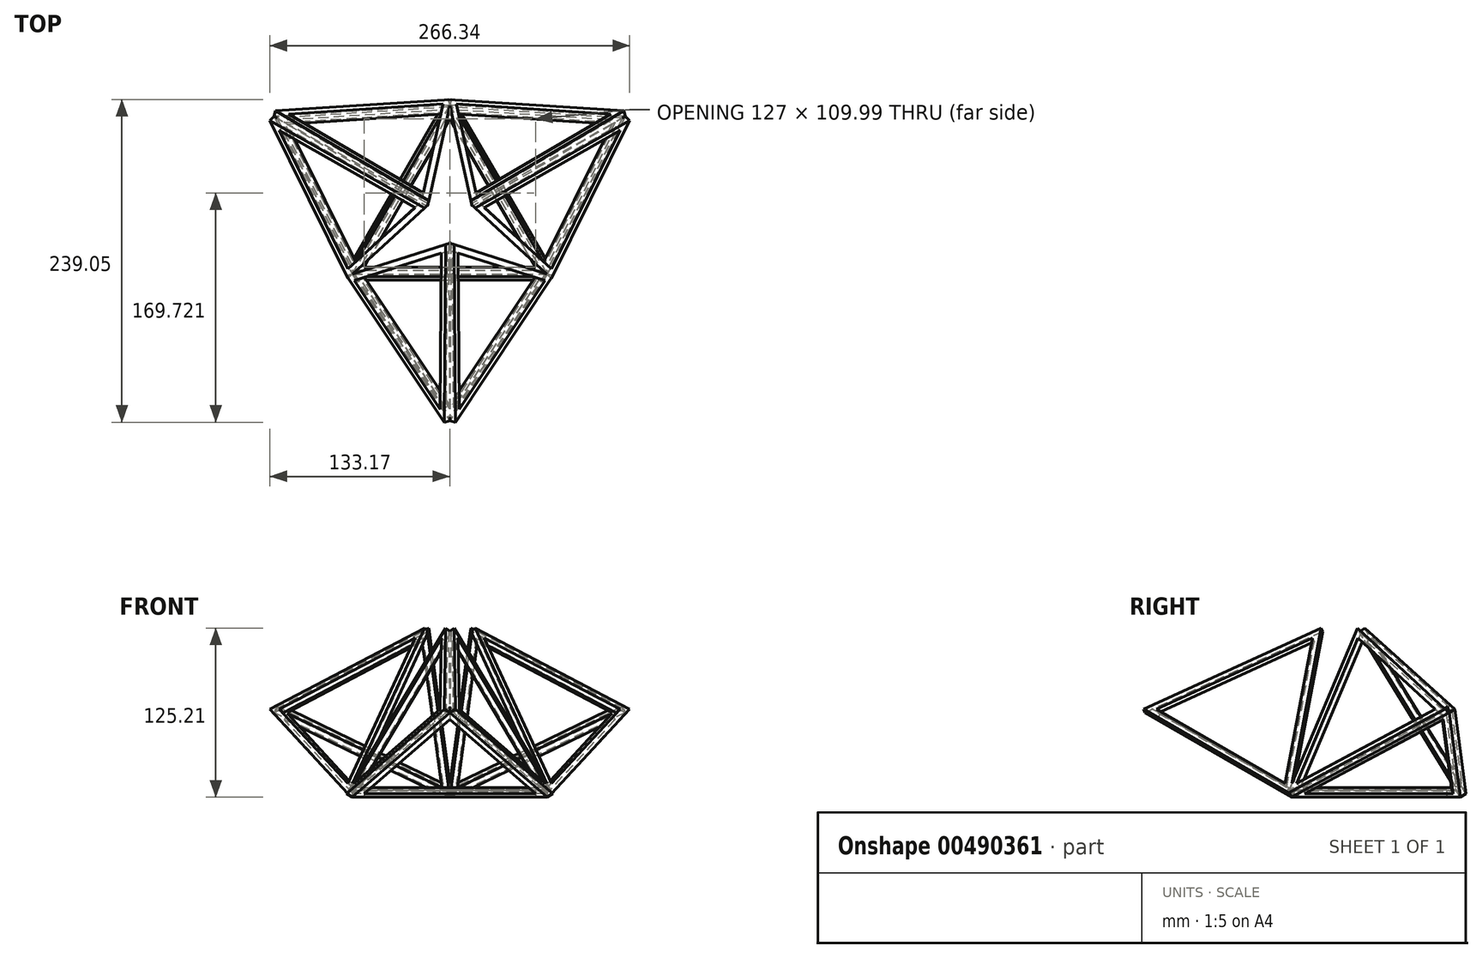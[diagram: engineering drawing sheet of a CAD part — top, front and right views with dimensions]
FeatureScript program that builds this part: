
annotation { "Feature Type Name" : "Feature", "Feature Type Description" : "" }
export const myFeature = defineFeature(function(context is Context, id is Id, definition is map)
    precondition{}
    {
        {
            var Q0;
            Q0=qCreatedBy(makeId("Top.planeOp"),FACE);
            var sketch = newSketch(context, id + "F0", { "sketchPlane" : qUnion([Q0])});
            skLineSegment(sketch, "E0", {"start": v(0, 73.32) * mm, "end": v(-63.5, -36.66) * mm});
            skLineSegment(sketch, "E1", {"start": v(-63.5, -36.66) * mm, "end": v(63.5, -36.66) * mm});
            skLineSegment(sketch, "E2", {"start": v(63.5, -36.66) * mm, "end": v(0, 73.32) * mm});
            skLineSegment(sketch, "E3", {"start": v(0, 83.48) * mm, "end": v(-72.3, -41.74) * mm});
            skLineSegment(sketch, "E4", {"start": v(-72.3, -41.74) * mm, "end": v(72.3, -41.74) * mm});
            skLineSegment(sketch, "E5", {"start": v(72.3, -41.74) * mm, "end": v(0, 83.48) * mm});
            skLineSegment(sketch, "E6", {"start": v(-31.75, 18.33) * mm, "end": v(63.5, -36.66) * mm, "construction": true});
            skLineSegment(sketch, "E7", {"start": v(31.75, 18.33) * mm, "end": v(-63.5, -36.66) * mm, "construction": true});
            skPoint(sketch, "E8", {"position": v(0, 0) * mm});
            skSolve(sketch);
        }
        {
            var Q0;
            Q0 = qSketchRegion(id + "F0", true);
            extrude(context, id + "F1", {"entities" : qUnion([Q0]), "depth" : 5.08 * mm});
        }
        {
            var Q0;
            Q0=makeQuery(id+"F1.opExtrude","CAP_EDGE",EDGE,{"disambiguationData":[OSD([sQuery(id+"F0.wireOp",EDGE,"E3")])],"isStart":true});
            var Q1;
            Q1=qCreatedBy(makeId("Top.planeOp"),FACE);
            cPlane(context, id + "F2", {"entities" : qUnion([Q0, Q1]), "cplaneType" : CPlaneType.LINE_ANGLE, "offset" : 25.4 * mm, "angle" : 30 * degree, "oppositeDirection" : true, "width" : 152.4 * mm, "height" : 152.4 * mm});
        }
        {
            var Q0;
            Q0=qCreatedBy(id+"F2.planeOp",FACE);
            var sketch = newSketch(context, id + "F3", { "sketchPlane" : qUnion([Q0])});
            skLineSegment(sketch, "E9.0", {"start": v(10.03, -80.2) * mm, "end": v(-70.18, 40.1) * mm});
            skLineSegment(sketch, "E10", {"start": v(-30.08, -20.05) * mm, "end": v(-171.97, -114.65) * mm, "construction": true});
            skLineSegment(sketch, "E11", {"start": v(10.03, -80.2) * mm, "end": v(-134.27, -89.51) * mm});
            skLineSegment(sketch, "E12", {"start": v(-134.27, -89.51) * mm, "end": v(-70.18, 40.1) * mm});
            skLineSegment(sketch, "E13", {"start": v(-125.82, -83.88) * mm, "end": v(0.92, -75.7) * mm});
            skLineSegment(sketch, "E14", {"start": v(0.92, -75.7) * mm, "end": v(-69.53, 29.97) * mm});
            skLineSegment(sketch, "E15", {"start": v(-69.53, 29.97) * mm, "end": v(-125.82, -83.88) * mm});
            skSolve(sketch);
        }
        {
            var Q0;
            Q0 = qSketchRegion(id + "F3", true);
            extrude(context, id + "F4", {"entities" : qUnion([Q0]), "oppositeDirection" : true, "depth" : 5.08 * mm});
        }
        {
            var Q0;
            Q0=makeQuery(id+"F1.opExtrude","CAP_EDGE",EDGE,{"disambiguationData":[OSD([sQuery(id+"F0.wireOp",EDGE,"E4")])],"isStart":true});
            var Q1;
            Q1=qCreatedBy(makeId("Top.planeOp"),FACE);
            cPlane(context, id + "F5", {"entities" : qUnion([Q0, Q1]), "cplaneType" : CPlaneType.LINE_ANGLE, "offset" : 25.4 * mm, "angle" : 30 * degree, "oppositeDirection" : true, "width" : 152.4 * mm, "height" : 152.4 * mm});
        }
        {
            var Q0;
            Q0=qCreatedBy(id+"F5.planeOp",FACE);
            var sketch = newSketch(context, id + "F6", { "sketchPlane" : qUnion([Q0])});
            skLineSegment(sketch, "E16.0", {"start": v(72.3, 36.15) * mm, "end": v(0, 161.37) * mm});
            skLineSegment(sketch, "E17", {"start": v(36.15, 98.76) * mm, "end": v(-111.54, 13.5) * mm, "construction": true});
            skLineSegment(sketch, "E18", {"start": v(72.3, 36.15) * mm, "end": v(-72.3, 36.15) * mm});
            skLineSegment(sketch, "E19", {"start": v(-72.3, 36.15) * mm, "end": v(0, 161.37) * mm});
            skLineSegment(sketch, "E20", {"start": v(-63.5, 41.23) * mm, "end": v(63.5, 41.23) * mm});
            skLineSegment(sketch, "E21", {"start": v(63.5, 41.23) * mm, "end": v(0, 151.21) * mm});
            skLineSegment(sketch, "E22", {"start": v(0, 151.21) * mm, "end": v(-63.5, 41.23) * mm});
            skSolve(sketch);
        }
        {
            var Q0;
            Q0 = qSketchRegion(id + "F6", true);
            extrude(context, id + "F7", {"entities" : qUnion([Q0]), "oppositeDirection" : true, "depth" : 5.08 * mm});
        }
        {
            var Q0;
            Q0=makeQuery(id+"F1.opExtrude","CAP_EDGE",EDGE,{"disambiguationData":[OSD([sQuery(id+"F0.wireOp",EDGE,"E5")])],"isStart":true});
            var Q1;
            Q1=qCreatedBy(makeId("Top.planeOp"),FACE);
            cPlane(context, id + "F8", {"entities" : qUnion([Q0, Q1]), "cplaneType" : CPlaneType.LINE_ANGLE, "offset" : 25.4 * mm, "angle" : 30 * degree, "oppositeDirection" : true, "width" : 152.4 * mm, "height" : 152.4 * mm});
        }
        {
            var Q0;
            Q0=qCreatedBy(id+"F8.planeOp",FACE);
            var sketch = newSketch(context, id + "F9", { "sketchPlane" : qUnion([Q0])});
            skLineSegment(sketch, "E23.0", {"start": v(134.27, -89.51) * mm, "end": v(70.18, 40.1) * mm});
            skLineSegment(sketch, "E24", {"start": v(102.23, -24.7) * mm, "end": v(-50.34, -100.14) * mm, "construction": true});
            skLineSegment(sketch, "E25", {"start": v(134.27, -89.51) * mm, "end": v(-10.03, -80.2) * mm});
            skLineSegment(sketch, "E26", {"start": v(-10.03, -80.2) * mm, "end": v(70.18, 40.1) * mm});
            skLineSegment(sketch, "E27", {"start": v(-0.92, -75.7) * mm, "end": v(125.82, -83.88) * mm});
            skLineSegment(sketch, "E28", {"start": v(125.82, -83.88) * mm, "end": v(69.53, 29.97) * mm});
            skLineSegment(sketch, "E29", {"start": v(69.53, 29.97) * mm, "end": v(-0.92, -75.7) * mm});
            skSolve(sketch);
        }
        {
            var Q0;
            Q0 = qSketchRegion(id + "F9", true);
            extrude(context, id + "F10", {"entities" : qUnion([Q0]), "oppositeDirection" : true, "depth" : 5.08 * mm});
        }
        {
            var Q0;
            Q0=makeQuery(id+"F10.opExtrude","SWEPT_BODY",BODY,{"disambiguationData":[OSD([sQuery(id+"F9.wireOp",EDGE,"E23.0"),sQuery(id+"F9.wireOp",EDGE,"E25"),sQuery(id+"F9.wireOp",EDGE,"E26"),sQuery(id+"F9.wireOp",EDGE,"E27"),sQuery(id+"F9.wireOp",EDGE,"E28"),sQuery(id+"F9.wireOp",EDGE,"E29")])]});
            var Q1;
            Q1=makeQuery(id+"F10.opExtrude","CAP_EDGE",EDGE,{"disambiguationData":[OSD([sQuery(id+"F9.wireOp",EDGE,"E23.0")])],"isStart":true});
            transform(context, id + "F11", {"entities" : qUnion([Q0]), "transformType" : TransformType.ROTATION, "transformAxis" : qUnion([Q1]), "angle" : 70 * degree, "oppositeDirection" : true, "makeCopy" : true});
        }
        {
            var Q0;
            Q0=makeQuery(id+"F10.opExtrude","SWEPT_BODY",BODY,{"disambiguationData":[OSD([sQuery(id+"F9.wireOp",EDGE,"E23.0"),sQuery(id+"F9.wireOp",EDGE,"E25"),sQuery(id+"F9.wireOp",EDGE,"E26"),sQuery(id+"F9.wireOp",EDGE,"E27"),sQuery(id+"F9.wireOp",EDGE,"E28"),sQuery(id+"F9.wireOp",EDGE,"E29")])]});
            var Q1;
            Q1=makeQuery(id+"F10.opExtrude","CAP_EDGE",EDGE,{"disambiguationData":[OSD([sQuery(id+"F9.wireOp",EDGE,"E25")])],"isStart":true});
            transform(context, id + "F12", {"entities" : qUnion([Q0]), "transformType" : TransformType.ROTATION, "transformAxis" : qUnion([Q1]), "angle" : 70 * degree, "makeCopy" : true});
        }
        {
            var Q0;
            Q0=makeQuery(id+"F7.opExtrude","SWEPT_BODY",BODY,{"disambiguationData":[OSD([sQuery(id+"F6.wireOp",EDGE,"E16.0"),sQuery(id+"F6.wireOp",EDGE,"E18"),sQuery(id+"F6.wireOp",EDGE,"E19"),sQuery(id+"F6.wireOp",EDGE,"E20"),sQuery(id+"F6.wireOp",EDGE,"E21"),sQuery(id+"F6.wireOp",EDGE,"E22")])]});
            var Q1;
            Q1=makeQuery(id+"F7.opExtrude","CAP_EDGE",EDGE,{"disambiguationData":[OSD([sQuery(id+"F6.wireOp",EDGE,"E19")])],"isStart":true});
            transform(context, id + "F13", {"entities" : qUnion([Q0]), "transformType" : TransformType.ROTATION, "transformAxis" : qUnion([Q1]), "angle" : 70 * degree, "makeCopy" : true});
        }
        {
            var Q0;
            Q0=makeQuery(id+"F7.opExtrude","SWEPT_BODY",BODY,{"disambiguationData":[OSD([sQuery(id+"F6.wireOp",EDGE,"E16.0"),sQuery(id+"F6.wireOp",EDGE,"E18"),sQuery(id+"F6.wireOp",EDGE,"E19"),sQuery(id+"F6.wireOp",EDGE,"E20"),sQuery(id+"F6.wireOp",EDGE,"E21"),sQuery(id+"F6.wireOp",EDGE,"E22")])]});
            var Q1;
            Q1=makeQuery(id+"F7.opExtrude","CAP_EDGE",EDGE,{"disambiguationData":[OSD([sQuery(id+"F6.wireOp",EDGE,"E16.0")])],"isStart":true});
            transform(context, id + "F14", {"entities" : qUnion([Q0]), "transformType" : TransformType.ROTATION, "transformAxis" : qUnion([Q1]), "angle" : 70 * degree, "oppositeDirection" : true, "makeCopy" : true});
        }
        {
            var Q0;
            Q0=makeQuery(id+"F4.opExtrude","SWEPT_BODY",BODY,{"disambiguationData":[OSD([sQuery(id+"F3.wireOp",EDGE,"E9.0"),sQuery(id+"F3.wireOp",EDGE,"E11"),sQuery(id+"F3.wireOp",EDGE,"E12"),sQuery(id+"F3.wireOp",EDGE,"E13"),sQuery(id+"F3.wireOp",EDGE,"E14"),sQuery(id+"F3.wireOp",EDGE,"E15")])]});
            var Q1;
            Q1=makeQuery(id+"F4.opExtrude","CAP_EDGE",EDGE,{"disambiguationData":[OSD([sQuery(id+"F3.wireOp",EDGE,"E12")])],"isStart":true});
            transform(context, id + "F15", {"entities" : qUnion([Q0]), "transformType" : TransformType.ROTATION, "transformAxis" : qUnion([Q1]), "angle" : 70 * degree, "makeCopy" : true});
        }
        {
            var Q0;
            Q0=makeQuery(id+"F4.opExtrude","SWEPT_BODY",BODY,{"disambiguationData":[OSD([sQuery(id+"F3.wireOp",EDGE,"E9.0"),sQuery(id+"F3.wireOp",EDGE,"E11"),sQuery(id+"F3.wireOp",EDGE,"E12"),sQuery(id+"F3.wireOp",EDGE,"E13"),sQuery(id+"F3.wireOp",EDGE,"E14"),sQuery(id+"F3.wireOp",EDGE,"E15")])]});
            var Q1;
            Q1=makeQuery(id+"F4.opExtrude","CAP_EDGE",EDGE,{"disambiguationData":[OSD([sQuery(id+"F3.wireOp",EDGE,"E11")])],"isStart":true});
            transform(context, id + "F16", {"entities" : qUnion([Q0]), "transformType" : TransformType.ROTATION, "transformAxis" : qUnion([Q1]), "angle" : 70 * degree, "makeCopy" : true});
        }
        {
            var Q0;
            Q0=makeQuery(id+"F7.opExtrude","CAP_FACE",FACE,{"disambiguationData":[OSD([sQuery(id+"F6.wireOp",EDGE,"E16.0"),sQuery(id+"F6.wireOp",EDGE,"E18"),sQuery(id+"F6.wireOp",EDGE,"E19"),sQuery(id+"F6.wireOp",EDGE,"E20"),sQuery(id+"F6.wireOp",EDGE,"E21"),sQuery(id+"F6.wireOp",EDGE,"E22")])],"isStart":true});
            var Q1;
            Q1=makeQuery(id+"F7.opExtrude","CAP_EDGE",EDGE,{"disambiguationData":[OSD([sQuery(id+"F6.wireOp",EDGE,"E21")])],"isStart":true});
            var Q2;
            Q2=makeQuery(id+"F7.opExtrude","CAP_EDGE",EDGE,{"disambiguationData":[OSD([sQuery(id+"F6.wireOp",EDGE,"E22")])],"isStart":true});
            loft(context, id + "F17", {"bodyType" : ToolBodyType.SURFACE, "sheetProfilesArray" : [{ "sheetProfileEntities" : qUnion([Q0]) }], "wireProfilesArray" : [{ "wireProfileEntities" : qUnion([Q1]) }, { "wireProfileEntities" : qUnion([Q2]) }]});
        }
        {
            var Q0;
            Q0=makeQuery(id+"F4.opExtrude","CAP_FACE",FACE,{"disambiguationData":[OSD([sQuery(id+"F3.wireOp",EDGE,"E9.0"),sQuery(id+"F3.wireOp",EDGE,"E11"),sQuery(id+"F3.wireOp",EDGE,"E12"),sQuery(id+"F3.wireOp",EDGE,"E13"),sQuery(id+"F3.wireOp",EDGE,"E14"),sQuery(id+"F3.wireOp",EDGE,"E15")])],"isStart":true});
            var Q1;
            Q1=makeQuery(id+"F4.opExtrude","CAP_EDGE",EDGE,{"disambiguationData":[OSD([sQuery(id+"F3.wireOp",EDGE,"E15")])],"isStart":true});
            var Q2;
            Q2=makeQuery(id+"F4.opExtrude","CAP_EDGE",EDGE,{"disambiguationData":[OSD([sQuery(id+"F3.wireOp",EDGE,"E13")])],"isStart":true});
            loft(context, id + "F18", {"bodyType" : ToolBodyType.SURFACE, "sheetProfilesArray" : [{ "sheetProfileEntities" : qUnion([Q0]) }], "wireProfilesArray" : [{ "wireProfileEntities" : qUnion([Q1]) }, { "wireProfileEntities" : qUnion([Q2]) }]});
        }
        {
            var Q0;
            Q0=makeQuery(id+"F10.opExtrude","CAP_FACE",FACE,{"disambiguationData":[OSD([sQuery(id+"F9.wireOp",EDGE,"E23.0"),sQuery(id+"F9.wireOp",EDGE,"E25"),sQuery(id+"F9.wireOp",EDGE,"E26"),sQuery(id+"F9.wireOp",EDGE,"E27"),sQuery(id+"F9.wireOp",EDGE,"E28"),sQuery(id+"F9.wireOp",EDGE,"E29")])],"isStart":true});
            var Q1;
            Q1=makeQuery(id+"F10.opExtrude","CAP_EDGE",EDGE,{"disambiguationData":[OSD([sQuery(id+"F9.wireOp",EDGE,"E27")])],"isStart":true});
            var Q2;
            Q2=makeQuery(id+"F10.opExtrude","CAP_EDGE",EDGE,{"disambiguationData":[OSD([sQuery(id+"F9.wireOp",EDGE,"E28")])],"isStart":true});
            loft(context, id + "F19", {"bodyType" : ToolBodyType.SURFACE, "sheetProfilesArray" : [{ "sheetProfileEntities" : qUnion([Q0]) }], "wireProfilesArray" : [{ "wireProfileEntities" : qUnion([Q1]) }, { "wireProfileEntities" : qUnion([Q2]) }]});
        }
        {
            var Q0;
            Q0=makeQuery(id+"F11.opPattern","COPY",EDGE,{"derivedFrom":makeQuery(id+"F10.opExtrude","CAP_EDGE",EDGE,{"disambiguationData":[OSD([sQuery(id+"F9.wireOp",EDGE,"E27")])],"isStart":false}),"instanceName":"1"});
            var Q1;
            Q1=makeQuery(id+"F11.opPattern","COPY",EDGE,{"derivedFrom":makeQuery(id+"F10.opExtrude","CAP_EDGE",EDGE,{"disambiguationData":[OSD([sQuery(id+"F9.wireOp",EDGE,"E29")])],"isStart":false}),"instanceName":"1"});
            loft(context, id + "F20", {"bodyType" : ToolBodyType.SURFACE, "wireProfilesArray" : [{ "wireProfileEntities" : qUnion([Q0]) }, { "wireProfileEntities" : qUnion([Q1]) }]});
        }
        {
            var Q0;
            Q0=makeQuery(id+"F14.opPattern","COPY",EDGE,{"derivedFrom":makeQuery(id+"F7.opExtrude","CAP_EDGE",EDGE,{"disambiguationData":[OSD([sQuery(id+"F6.wireOp",EDGE,"E20")])],"isStart":false}),"instanceName":"1"});
            var Q1;
            Q1=makeQuery(id+"F14.opPattern","COPY",EDGE,{"derivedFrom":makeQuery(id+"F7.opExtrude","CAP_EDGE",EDGE,{"disambiguationData":[OSD([sQuery(id+"F6.wireOp",EDGE,"E22")])],"isStart":false}),"instanceName":"1"});
            loft(context, id + "F21", {"bodyType" : ToolBodyType.SURFACE, "wireProfilesArray" : [{ "wireProfileEntities" : qUnion([Q0]) }, { "wireProfileEntities" : qUnion([Q1]) }]});
        }
        {
            var Q0;
            Q0=makeQuery(id+"F13.opPattern","COPY",EDGE,{"derivedFrom":makeQuery(id+"F7.opExtrude","CAP_EDGE",EDGE,{"disambiguationData":[OSD([sQuery(id+"F6.wireOp",EDGE,"E20")])],"isStart":false}),"instanceName":"1"});
            var Q1;
            Q1=makeQuery(id+"F13.opPattern","COPY",EDGE,{"derivedFrom":makeQuery(id+"F7.opExtrude","CAP_EDGE",EDGE,{"disambiguationData":[OSD([sQuery(id+"F6.wireOp",EDGE,"E21")])],"isStart":false}),"instanceName":"1"});
            loft(context, id + "F22", {"bodyType" : ToolBodyType.SURFACE, "wireProfilesArray" : [{ "wireProfileEntities" : qUnion([Q0]) }, { "wireProfileEntities" : qUnion([Q1]) }]});
        }
        {
            var Q0;
            Q0=makeQuery(id+"F15.opPattern","COPY",EDGE,{"derivedFrom":makeQuery(id+"F4.opExtrude","CAP_EDGE",EDGE,{"disambiguationData":[OSD([sQuery(id+"F3.wireOp",EDGE,"E14")])],"isStart":false}),"instanceName":"1"});
            var Q1;
            Q1=makeQuery(id+"F15.opPattern","COPY",EDGE,{"derivedFrom":makeQuery(id+"F4.opExtrude","CAP_EDGE",EDGE,{"disambiguationData":[OSD([sQuery(id+"F3.wireOp",EDGE,"E13")])],"isStart":false}),"instanceName":"1"});
            loft(context, id + "F23", {"bodyType" : ToolBodyType.SURFACE, "wireProfilesArray" : [{ "wireProfileEntities" : qUnion([Q0]) }, { "wireProfileEntities" : qUnion([Q1]) }]});
        }
    });
